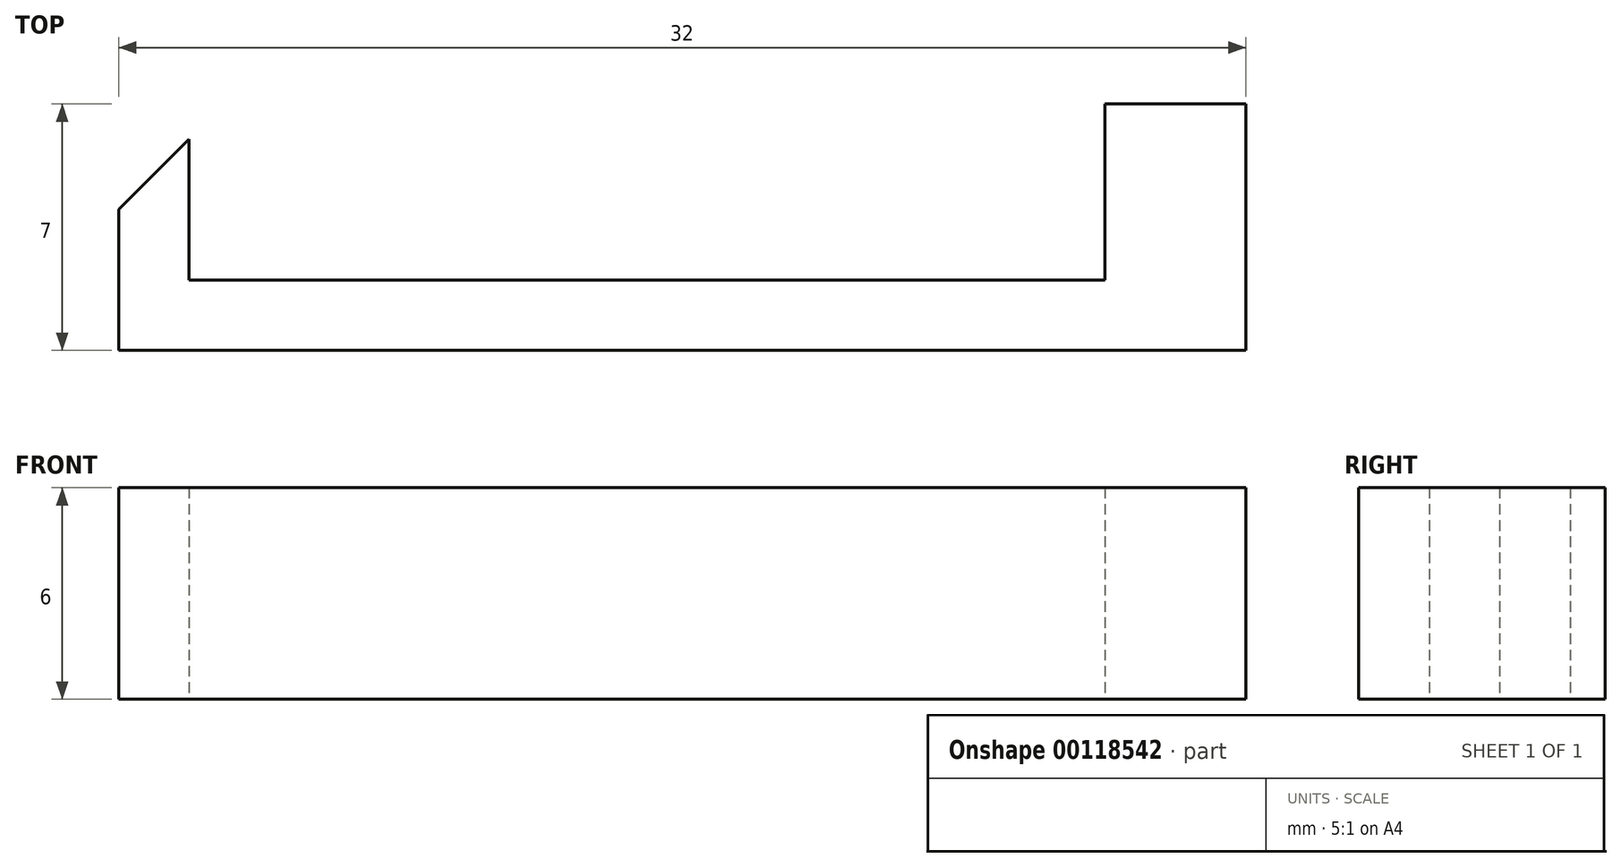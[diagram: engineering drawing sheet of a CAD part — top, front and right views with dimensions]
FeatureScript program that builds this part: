
annotation { "Feature Type Name" : "Feature", "Feature Type Description" : "" }
export const myFeature = defineFeature(function(context is Context, id is Id, definition is map)
    precondition{}
    {
        {
            var Q0;
            Q0=qCreatedBy(makeId("Top.planeOp"),FACE);
            var sketch = newSketch(context, id + "F0", { "sketchPlane" : qUnion([Q0])});
            skLineSegment(sketch, "E0", {"start": v(-4, 2) * mm, "end": v(-4, 7) * mm});
            skLineSegment(sketch, "E1", {"start": v(-4, 7) * mm, "end": v(0, 7) * mm});
            skLineSegment(sketch, "E2", {"start": v(0, 7) * mm, "end": v(0, 0) * mm});
            skLineSegment(sketch, "E3", {"start": v(0, 0) * mm, "end": v(-32, 0) * mm});
            skLineSegment(sketch, "E4", {"start": v(-32, 0) * mm, "end": v(-32, 6) * mm});
            skLineSegment(sketch, "E5", {"start": v(-4, 2) * mm, "end": v(-30, 2) * mm});
            skLineSegment(sketch, "E6", {"start": v(-30, 2) * mm, "end": v(-30, 6) * mm});
            skLineSegment(sketch, "E7", {"start": v(-30, 6) * mm, "end": v(-32, 6) * mm});
            skSolve(sketch);
        }
        {
            var Q0;
            Q0=makeQuery(id+"F0.imprint","IMPRINT",FACE,{"disambiguationData":[TD([[makeQuery(id+"F0.imprint","IMPRINT",EDGE,{"derivedFrom":sQuery(id+"F0.wireOp",EDGE,"E0")}),-1.0]])]});
            extrude(context, id + "F1", {"entities" : qUnion([Q0]), "depth" : 6 * mm});
        }
        {
            var Q0;
            Q0=makeQuery(id+"F1.opExtrude","SWEPT_EDGE",EDGE,{"disambiguationData":[OSD([sQuery(id+"F0.wireOp",EDGE,"E4"),sQuery(id+"F0.wireOp",EDGE,"E7")])]});
            chamfer(context, id + "F2", {"entities" : qUnion([Q0]), "width" : 2 * mm, "tangentPropagation" : true});
        }
    });
